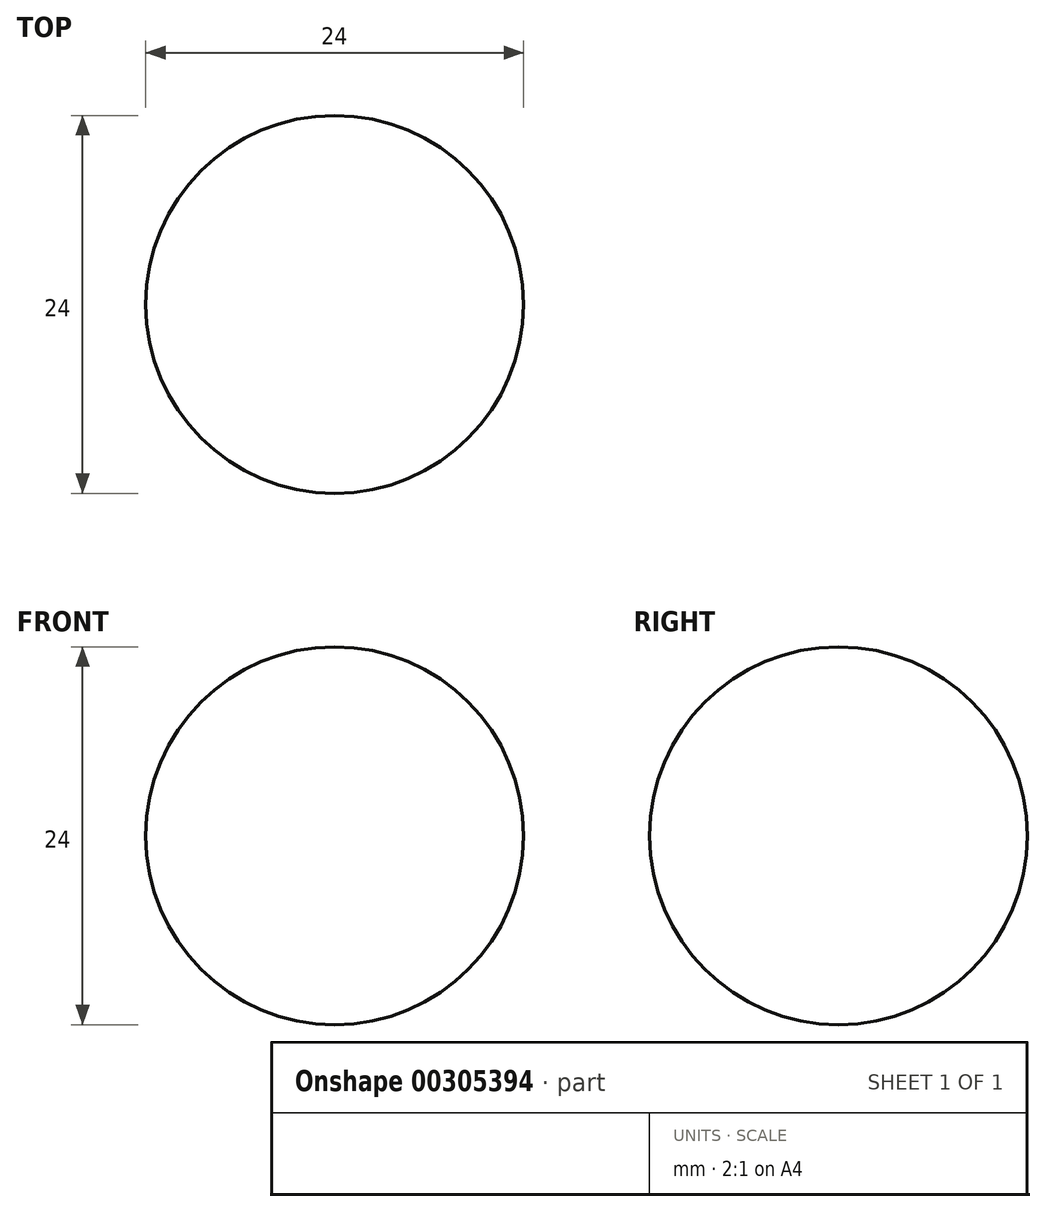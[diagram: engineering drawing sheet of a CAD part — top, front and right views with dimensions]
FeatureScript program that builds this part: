
annotation { "Feature Type Name" : "Feature", "Feature Type Description" : "" }
export const myFeature = defineFeature(function(context is Context, id is Id, definition is map)
    precondition{}
    {
        {
            var Q0;
            Q0=qCreatedBy(makeId("Front.planeOp"),FACE);
            var sketch = newSketch(context, id + "F0", { "sketchPlane" : qUnion([Q0])});
            skLineSegment(sketch, "E0", {"start": v(0, 12) * mm, "end": v(0, -12) * mm});
            skPoint(sketch, "E1", {"position": v(0, 0) * mm});
            skArc(sketch, "E2", {"start": v(0, 12) * mm, "mid": v(-12, 0) * mm, "end": v(0, -12) * mm});
            skSolve(sketch);
        }
        {
            var Q0;
            Q0 = qSketchRegion(id + "F0", true);
            var Q1;
            Q1=sQuery(id+"F0.wireOp",EDGE,"E0");
            revolve(context, id + "F1", {"entities" : qUnion([Q0]), "axis" : qUnion([Q1]), "revolveType" : RevolveType.FULL});
        }
    });
